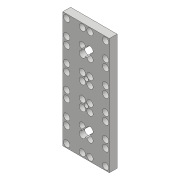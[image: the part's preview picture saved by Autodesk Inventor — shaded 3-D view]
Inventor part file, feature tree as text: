
AUTODESK INVENTOR PART (.ipt)
format: ipt  version: 2018 (Build 220112000, 112)  size: 624,128 bytes
history: native  units: mm
features: projected_geometry x10, extrude x9, sketch x8, pattern_linear x6, fillet x5
ambient origin geometry x8: Origin, YZ Plane, XZ Plane, XY Plane, X Axis, Y Axis, Z Axis, Center Point
bodies: Solid1 (feature_tree)
feature tree (38):
  extrude  "Extrusion1"  Depth=44.0mm
  extrude  "Extrusion2"  Depth=22.0mm
  extrude  "Extrusion3"  Depth=22.0mm
  pattern_linear  "Rectangular Pattern1"  Spacing1=6.0mm  [1 undecoded]
  extrude  "Extrusion4"  Depth=6.0mm
  pattern_linear  "Rectangular Pattern2"  Count1=5 Spacing1=22.0mm
  extrude  "Extrusion5"  Depth=22.0mm
  pattern_linear  "Rectangular Pattern3"  Spacing1=10.0mm  [1 undecoded]
  fillet  "Fillet1"  Radius=5.0mm
  extrude  "Extrusion6"  Depth=5.0mm
  extrude  "Extrusion9"  Depth=5.0mm
  pattern_linear  "Rectangular Pattern4"  Spacing1=2.0mm  [1 undecoded]
  extrude  "Extrusion7"  Depth=50.0mm
  pattern_linear  "Rectangular Pattern5"  Spacing1=2.0mm  [1 undecoded]
  pattern_linear  "Rectangular Pattern6"  Count1=2 Spacing1=22.0mm
  fillet  "Fillet2"  Radius=1.0mm
  fillet  "Fillet3"  Radius=8.5mm
  fillet  "Fillet4"  Radius=6.7mm
  extrude  "Extrusion8"  Depth=66.0mm
  fillet  "Fillet5"  Radius=4.0mm
  sketch  "Sketch1"  dims[d0=110.0mm d1=44.0mm]
  sketch  "Sketch2"  dims[d2=7.3mm d3=0.0mm d4=22.0mm]
  projected_geometry  "Projected Loop1"
  sketch  "Sketch3"  dims[d5=22.0mm d6=14.75mm]
  projected_geometry  "Projected Loop2"
  projected_geometry  "Projected Loop3"
  projected_geometry  "Projected Loop4"
  projected_geometry  "Projected Loop5"
  sketch  "Sketch4"  dims[d7=7.5mm]
  projected_geometry  "Projected Loop6"
  sketch  "Sketch5"  dims[d8=7.0mm d9=0.0mm]
  projected_geometry  "Projected Loop7"
  projected_geometry  "Projected Loop8"
  sketch  "Sketch7"  dims[d10=6.7mm d11=0.0mm]
  projected_geometry  "Projected Loop9"
  sketch  "Sketch8"  dims[d12=6.0mm]
  projected_geometry  "Projected Loop10"
  sketch  "Sketch9"  dims[d13=6.0mm d14=6.0mm d15=6.0mm d16=50.0mm d18=22.0mm d19=20.0mm d21=22.0mm d22=10.0mm d23=5.0mm d24=5.0mm d25=5.0mm d26=2.0mm d27=0.0mm d28=50.0mm d30=22.0mm d31=2.0mm d32=0.0mm d33=20.0mm d35=22.0mm d36=1.0mm d37=8.5mm d38=6.7mm d39=0.0mm d40=20.0mm d42=66.0mm d43=4.0mm d44=2.0mm d45=0.0mm d46=20.0mm d48=22.0mm d49=4.0mm d50=0.5mm d51=1.0mm d52=2.5mm d53=3.0mm d54=0.0mm d55=0.5mm d56=2.0mm d57=2.0mm d58=2.0mm d59=2.0mm d60=2.0mm d61=2.0mm d62=2.0mm d63=2.0mm d64=10.0mm d65=0.0mm d66=40.0mm d68=22.0mm]
note: 4 required parameter values undecoded (feature->parameter linkage not recoverable at this tier; creation-order binding heuristic only, values carry confidence <= 0.55)
